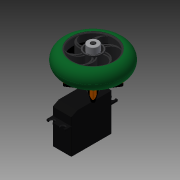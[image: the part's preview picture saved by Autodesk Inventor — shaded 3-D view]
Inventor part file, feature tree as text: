
AUTODESK INVENTOR PART (.ipt)
format: ipt  version: 2015 (Build 190159000, 159)  size: 1,143,808 bytes
history: native  units: in
note: dims shown in document units (in); Inventor stores cm internally (conversion verified against a paired STEP export)
features: sketch x28, extrude x22, mirror x7, fillet x3, sweep x2, chamfer x2, plane x2, projected_geometry x2, revolve x1
ambient origin geometry x8: Origin, YZ Plane, XZ Plane, XY Plane, X Axis, Y Axis, Z Axis, Center Point
bodies: Solid1 (feature_tree)
feature tree (69):
  sweep  "Sweep1"
  sketch  "Sketch3"  dims[d18=0.0625in d19=0.0in d20=0.25in d21=0.0in]
  sketch  "Sketch6"  dims[d22=0.0625in d23=0.0in d24=0.0625in d25=0.0in]
  extrude  "Extrusion4"  Depth=1.75in
  extrude  "Extrusion5"  Depth=0.25in TaperAngle=0.0deg
  extrude  "Extrusion6"  Depth=0.0625in TaperAngle=0.0deg
  mirror  "Mirror1"
  extrude  "Extrusion7"  Depth=0.25in TaperAngle=0.0deg
  mirror  "Mirror2"
  sketch  "Sketch11"  dims[d38=0.025in d39=0.125in d40=45.0deg d41=0.25in d42=0.0in]
  extrude  "Extrusion8"  Depth=0.0625in TaperAngle=0.0deg
  extrude  "Extrusion9"  Depth=0.65in TaperAngle=0.0deg
  mirror  "Mirror3"
  extrude  "Extrusion10"  Depth=0.25in TaperAngle=0.0deg
  mirror  "Mirror4"
  extrude  "Extrusion11"  Depth=0.1in TaperAngle=0.0deg
  mirror  "Mirror5"
  extrude  "Extrusion12"  Depth=0.02in
  mirror  "Mirror6"
  extrude  "Extrusion13"  Depth=0.4in TaperAngle=0.0deg
  chamfer  "Chamfer1"  Distance=0.1in
  extrude  "Extrusion14"  Depth=0.1in
  extrude  "Extrusion15"  TaperAngle=90.0deg  [1 undecoded]
  extrude  "Extrusion16"  Depth=0.01in TaperAngle=0.0deg
  fillet  "Fillet1"  Radius=0.375in
  extrude  "Extrusion17"  Depth=1.625in
  extrude  "Extrusion18"  Depth=1.5in TaperAngle=0.0deg
  extrude  "Extrusion19"  Depth=1.5in TaperAngle=0.0deg
  revolve  "Revolution1"  [1 undecoded]
  extrude  "Extrusion20"  Depth=0.0626in
  extrude  "Extrusion21"  Depth=0.2in
  extrude  "Extrusion22"  [1 undecoded]
  extrude  "Extrusion23"  Depth=0.025in
  chamfer  "Chamfer2"  [1 undecoded]
  extrude  "Extrusion24"  [1 undecoded]
  extrude  "Extrusion25"  [1 undecoded]
  plane  "Work Plane2"
  mirror  "Mirror7"
  fillet  "Fillet2"  [1 undecoded]
  fillet  "Fillet3"  [1 undecoded]
  plane  "Work Plane3"
  sweep  "Sweep2"
  sketch  "Sketch1"  dims[d0=2.5in d1=0.75in]
  sketch  "Sketch2"  dims[d2=0.0in d3=0.0in d4=1.75in]
  sketch  "Sketch7"  dims[d26=0.25in d27=0.0in d28=0.24in d29=0.0in]
  sketch  "Sketch9"  dims[d30=0.2in d31=0.0in d32=0.0625in d33=0.0in]
  sketch  "Sketch10"  dims[d34=0.05in d35=0.0in d36=0.65in d37=0.0in]
  sketch  "Sketch12"  dims[d43=0.1875in d44=0.1in d45=0.0in]
  sketch  "Sketch14"  dims[d46=0.58in d47=0.0in d48=0.02in]
  projected_geometry  "Projected Loop2"
  sketch  "Sketch15"  dims[d49=0.4in d50=0.0in d51=0.4in d52=0.0in d53=0.1in d54=0.0in]
  sketch  "Sketch16"  dims[d55=0.125in d60=0.1in]
  sketch  "Sketch18"  dims[d62=0.025in d63=90.0deg]
  sketch  "Sketch19"  dims[d64=0.17in d65=0.01in d66=0.0in d67=0.375in]
  sketch  "Sketch20"  dims[d68=0.0375in d69=0.0in d70=1.625in]
  sketch  "Sketch21"  dims[d71=0.75in d73=1.5in d74=0.0in]
  sketch  "Sketch22"  dims[d76=0.125in d77=1.5in d78=0.0in]
  projected_geometry  "Projected Loop4"
  sketch  "Sketch23"  dims[d79=0.03in d80=0.125in d81=45.0deg d90=0.5in]
  sketch  "Sketch24"  dims[d92=0.25in d93=0.0626in]
  sketch  "Sketch25"  dims[d94=0.75in d95=0.0in d97=0.2in]
  sketch  "Sketch26"  dims[d98=0.75in d99=0.0in d100=-0.8125in]
  sketch  "Sketch27"  dims[d101=0.01in d102=0.025in d103=0.0in d104=0.0in]
  sketch  "Sketch28"
  sketch  "Sketch29"
  sketch  "Sketch31"
  sketch  "Sketch32"
  sketch  "Sketch33"
  sketch  "Sketch34"
note: 8 required parameter values undecoded (feature->parameter linkage not recoverable at this tier; creation-order binding heuristic only, values carry confidence <= 0.55)